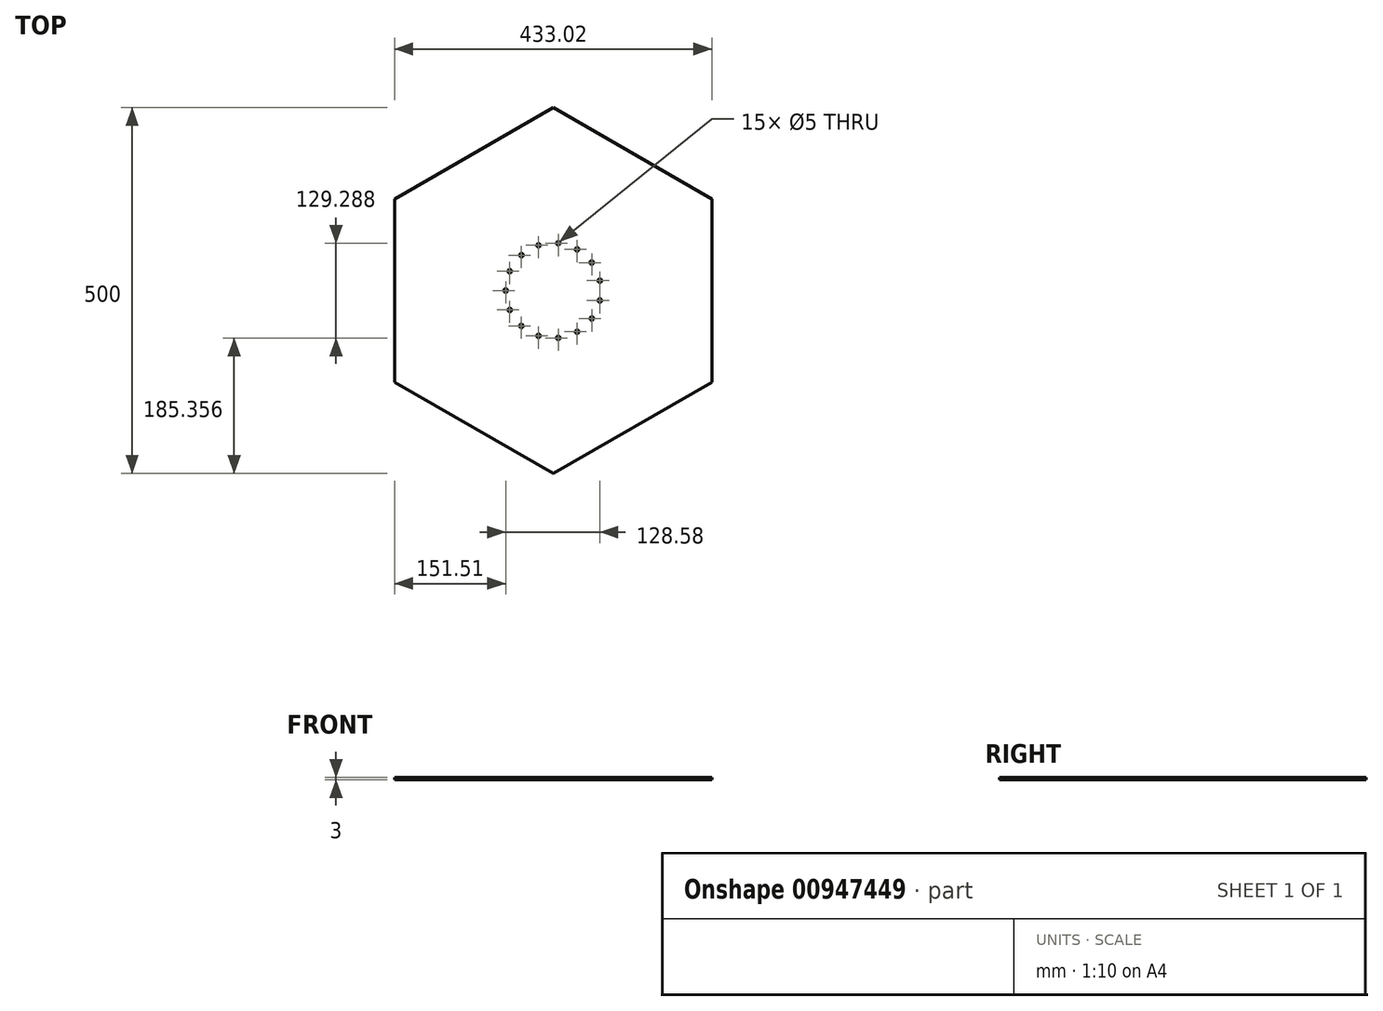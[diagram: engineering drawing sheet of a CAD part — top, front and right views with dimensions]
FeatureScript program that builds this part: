
annotation { "Feature Type Name" : "Feature", "Feature Type Description" : "" }
export const myFeature = defineFeature(function(context is Context, id is Id, definition is map)
    precondition{}
    {
        {
            var Q0;
            Q0=qCreatedBy(makeId("Top.planeOp"),FACE);
            var sketch = newSketch(context, id + "F0", { "sketchPlane" : qUnion([Q0])});
            skCircle(sketch, "E0", {"center": v(0, 0) * mm, "radius": 216.5 * mm});
            skCircle(sketch, "E1.cCircle", {"center": v(0, 0) * mm, "radius": 216.5 * mm, "construction": true});
            skLineSegment(sketch, "E1.0", {"start": v(216.5, 125) * mm, "end": v(216.5, -125) * mm});
            skLineSegment(sketch, "E1.1", {"start": v(216.5, -125) * mm, "end": v(0, -250) * mm});
            skLineSegment(sketch, "E1.2", {"start": v(0, -250) * mm, "end": v(-216.5, -125) * mm});
            skLineSegment(sketch, "E1.3", {"start": v(-216.5, -125) * mm, "end": v(-216.5, 125) * mm});
            skLineSegment(sketch, "E1.4", {"start": v(-216.5, 125) * mm, "end": v(0, 250) * mm});
            skLineSegment(sketch, "E1.5", {"start": v(0, 250) * mm, "end": v(216.5, 125) * mm});
            skPoint(sketch, "E1.0.midPoint", {"position": v(216.5, 0) * mm});
            skSolve(sketch);
        }
        {
            var Q0;
            Q0=makeQuery(id+"F0.imprint","IMPRINT",FACE,{"disambiguationData":[TD([[makeQuery(id+"F0.imprint","IMPRINT",EDGE,{"derivedFrom":sQuery(id+"F0.wireOp",EDGE,"E0")}),1.0]])]});
            var Q1;
            {var subQ0=sQuery(id+"F0.wireOp",EDGE,"E1.4");var subQ1=sQuery(id+"F0.wireOp",EDGE,"E0");var subQ2=makeQuery(id+"F0.imprint","INTERSECT",VERTEX,{"derivedFrom":[subQ1,subQ0]});Q1=makeQuery(id+"F0.imprint","IMPRINT",FACE,{"disambiguationData":[TD([[makeQuery(id+"F0.imprint","IMPRINT",EDGE,{"disambiguationData":[TD([[subQ2,-1.0]])],"derivedFrom":subQ1}),-1.0]])]});}
            var Q2;
            {var subQ0=sQuery(id+"F0.wireOp",EDGE,"E1.5");var subQ1=sQuery(id+"F0.wireOp",EDGE,"E0");var subQ2=makeQuery(id+"F0.imprint","INTERSECT",VERTEX,{"derivedFrom":[subQ1,subQ0]});Q2=makeQuery(id+"F0.imprint","IMPRINT",FACE,{"disambiguationData":[TD([[makeQuery(id+"F0.imprint","IMPRINT",EDGE,{"disambiguationData":[TD([[subQ2,-1.0]])],"derivedFrom":subQ1}),-1.0]])]});}
            var Q3;
            {var subQ0=sQuery(id+"F0.wireOp",EDGE,"E1.5");var subQ1=sQuery(id+"F0.wireOp",EDGE,"E0");var subQ2=makeQuery(id+"F0.imprint","INTERSECT",VERTEX,{"derivedFrom":[subQ1,subQ0]});Q3=makeQuery(id+"F0.imprint","IMPRINT",FACE,{"disambiguationData":[TD([[makeQuery(id+"F0.imprint","IMPRINT",EDGE,{"disambiguationData":[TD([[subQ2,1.0]])],"derivedFrom":subQ1}),-1.0]])]});}
            var Q4;
            {var subQ0=sQuery(id+"F0.wireOp",EDGE,"E1.0");var subQ1=sQuery(id+"F0.wireOp",EDGE,"E0");var subQ2=makeQuery(id+"F0.imprint","INTERSECT",VERTEX,{"derivedFrom":[subQ1,subQ0]});Q4=makeQuery(id+"F0.imprint","IMPRINT",FACE,{"disambiguationData":[TD([[makeQuery(id+"F0.imprint","IMPRINT",EDGE,{"disambiguationData":[TD([[subQ2,1.0]])],"derivedFrom":subQ1}),-1.0]])]});}
            var Q5;
            {var subQ0=sQuery(id+"F0.wireOp",EDGE,"E1.2");var subQ1=sQuery(id+"F0.wireOp",EDGE,"E0");var subQ2=makeQuery(id+"F0.imprint","INTERSECT",VERTEX,{"derivedFrom":[subQ1,subQ0]});Q5=makeQuery(id+"F0.imprint","IMPRINT",FACE,{"disambiguationData":[TD([[makeQuery(id+"F0.imprint","IMPRINT",EDGE,{"disambiguationData":[TD([[subQ2,-1.0]])],"derivedFrom":subQ1}),-1.0]])]});}
            var Q6;
            {var subQ0=sQuery(id+"F0.wireOp",EDGE,"E1.3");var subQ1=sQuery(id+"F0.wireOp",EDGE,"E0");var subQ2=makeQuery(id+"F0.imprint","INTERSECT",VERTEX,{"derivedFrom":[subQ1,subQ0]});Q6=makeQuery(id+"F0.imprint","IMPRINT",FACE,{"disambiguationData":[TD([[makeQuery(id+"F0.imprint","IMPRINT",EDGE,{"disambiguationData":[TD([[subQ2,-1.0]])],"derivedFrom":subQ1}),-1.0]])]});}
            extrude(context, id + "F1", {"entities" : qUnion([Q0, Q1, Q2, Q3, Q4, Q5, Q6]), "oppositeDirection" : true, "depth" : 3 * mm, "offsetDistance" : 25 * mm});
        }
        {
            var Q0;
            Q0=makeQuery(id+"F1.opExtrude","CAP_FACE",FACE,{"disambiguationData":[OSD([sQuery(id+"F0.wireOp",EDGE,"E1.0"),sQuery(id+"F0.wireOp",EDGE,"E1.1"),sQuery(id+"F0.wireOp",EDGE,"E1.2"),sQuery(id+"F0.wireOp",EDGE,"E1.3"),sQuery(id+"F0.wireOp",EDGE,"E1.4"),sQuery(id+"F0.wireOp",EDGE,"E1.5")])],"isStart":true});
            var sketch = newSketch(context, id + "F2", { "sketchPlane" : qUnion([Q0])});
            skCircle(sketch, "E2", {"center": v(0, 0) * mm, "radius": 65 * mm, "construction": true});
            skCircle(sketch, "E3", {"center": v(-65, 0) * mm, "radius": 2.5 * mm});
            skCircle(sketch, "E4.1.0", {"center": v(-59.38, -26.44) * mm, "radius": 2.5 * mm});
            skCircle(sketch, "E4.2.0", {"center": v(-43.5, -48.3) * mm, "radius": 2.5 * mm});
            skCircle(sketch, "E4.3.0", {"center": v(-20.09, -61.82) * mm, "radius": 2.5 * mm});
            skCircle(sketch, "E4.4.0", {"center": v(6.8, -64.64) * mm, "radius": 2.5 * mm});
            skCircle(sketch, "E4.5.0", {"center": v(32.5, -56.3) * mm, "radius": 2.5 * mm});
            skCircle(sketch, "E5.1.6.0", {"center": v(52.59, -38.2) * mm, "radius": 2.5 * mm});
            skCircle(sketch, "E5.1.7.0", {"center": v(63.58, -13.51) * mm, "radius": 2.5 * mm});
            skCircle(sketch, "E5.1.8.0", {"center": v(63.58, 13.51) * mm, "radius": 2.5 * mm});
            skCircle(sketch, "E5.1.9.0", {"center": v(52.59, 38.2) * mm, "radius": 2.5 * mm});
            skCircle(sketch, "E5.1.10.0", {"center": v(32.5, 56.3) * mm, "radius": 2.5 * mm});
            skCircle(sketch, "E5.1.11.0", {"center": v(6.8, 64.64) * mm, "radius": 2.5 * mm});
            skCircle(sketch, "E5.1.12.0", {"center": v(-20.09, 61.82) * mm, "radius": 2.5 * mm});
            skCircle(sketch, "E5.1.13.0", {"center": v(-43.5, 48.3) * mm, "radius": 2.5 * mm});
            skCircle(sketch, "E5.1.14.0", {"center": v(-59.38, 26.44) * mm, "radius": 2.5 * mm});
            skSolve(sketch);
        }
        {
            var Q0;
            Q0=makeQuery(id+"F2.imprint","IMPRINT",FACE,{"disambiguationData":[TD([[makeQuery(id+"F2.imprint","IMPRINT",EDGE,{"derivedFrom":sQuery(id+"F2.wireOp",EDGE,"E3")}),1.0]])]});
            var Q1;
            Q1=makeQuery(id+"F2.imprint","IMPRINT",FACE,{"disambiguationData":[TD([[makeQuery(id+"F2.imprint","IMPRINT",EDGE,{"derivedFrom":sQuery(id+"F2.wireOp",EDGE,"E4.5.0")}),1.0]])]});
            var Q2;
            Q2=makeQuery(id+"F2.imprint","IMPRINT",FACE,{"disambiguationData":[TD([[makeQuery(id+"F2.imprint","IMPRINT",EDGE,{"derivedFrom":sQuery(id+"F2.wireOp",EDGE,"E4.4.0")}),1.0]])]});
            var Q3;
            Q3=makeQuery(id+"F2.imprint","IMPRINT",FACE,{"disambiguationData":[TD([[makeQuery(id+"F2.imprint","IMPRINT",EDGE,{"derivedFrom":sQuery(id+"F2.wireOp",EDGE,"E4.3.0")}),1.0]])]});
            var Q4;
            Q4=makeQuery(id+"F2.imprint","IMPRINT",FACE,{"disambiguationData":[TD([[makeQuery(id+"F2.imprint","IMPRINT",EDGE,{"derivedFrom":sQuery(id+"F2.wireOp",EDGE,"E4.2.0")}),1.0]])]});
            var Q5;
            Q5=makeQuery(id+"F2.imprint","IMPRINT",FACE,{"disambiguationData":[TD([[makeQuery(id+"F2.imprint","IMPRINT",EDGE,{"derivedFrom":sQuery(id+"F2.wireOp",EDGE,"E4.1.0")}),1.0]])]});
            var Q6;
            Q6=makeQuery(id+"F2.imprint","IMPRINT",FACE,{"disambiguationData":[TD([[makeQuery(id+"F2.imprint","IMPRINT",EDGE,{"derivedFrom":sQuery(id+"F2.wireOp",EDGE,"E5.1.14.0")}),1.0]])]});
            var Q7;
            Q7=makeQuery(id+"F2.imprint","IMPRINT",FACE,{"disambiguationData":[TD([[makeQuery(id+"F2.imprint","IMPRINT",EDGE,{"derivedFrom":sQuery(id+"F2.wireOp",EDGE,"E5.1.13.0")}),1.0]])]});
            var Q8;
            Q8=makeQuery(id+"F2.imprint","IMPRINT",FACE,{"disambiguationData":[TD([[makeQuery(id+"F2.imprint","IMPRINT",EDGE,{"derivedFrom":sQuery(id+"F2.wireOp",EDGE,"E5.1.12.0")}),1.0]])]});
            var Q9;
            Q9=makeQuery(id+"F2.imprint","IMPRINT",FACE,{"disambiguationData":[TD([[makeQuery(id+"F2.imprint","IMPRINT",EDGE,{"derivedFrom":sQuery(id+"F2.wireOp",EDGE,"E5.1.11.0")}),1.0]])]});
            var Q10;
            Q10=makeQuery(id+"F2.imprint","IMPRINT",FACE,{"disambiguationData":[TD([[makeQuery(id+"F2.imprint","IMPRINT",EDGE,{"derivedFrom":sQuery(id+"F2.wireOp",EDGE,"E5.1.10.0")}),1.0]])]});
            var Q11;
            Q11=makeQuery(id+"F2.imprint","IMPRINT",FACE,{"disambiguationData":[TD([[makeQuery(id+"F2.imprint","IMPRINT",EDGE,{"derivedFrom":sQuery(id+"F2.wireOp",EDGE,"E5.1.9.0")}),1.0]])]});
            var Q12;
            Q12=makeQuery(id+"F2.imprint","IMPRINT",FACE,{"disambiguationData":[TD([[makeQuery(id+"F2.imprint","IMPRINT",EDGE,{"derivedFrom":sQuery(id+"F2.wireOp",EDGE,"E5.1.8.0")}),1.0]])]});
            var Q13;
            Q13=makeQuery(id+"F2.imprint","IMPRINT",FACE,{"disambiguationData":[TD([[makeQuery(id+"F2.imprint","IMPRINT",EDGE,{"derivedFrom":sQuery(id+"F2.wireOp",EDGE,"E5.1.7.0")}),1.0]])]});
            var Q14;
            Q14=makeQuery(id+"F2.imprint","IMPRINT",FACE,{"disambiguationData":[TD([[makeQuery(id+"F2.imprint","IMPRINT",EDGE,{"derivedFrom":sQuery(id+"F2.wireOp",EDGE,"E5.1.6.0")}),1.0]])]});
            extrude(context, id + "F3", {"entities" : qUnion([Q0, Q1, Q2, Q3, Q4, Q5, Q6, Q7, Q8, Q9, Q10, Q11, Q12, Q13, Q14]), "operationType" : NewBodyOperationType.REMOVE, "endBound" : BoundingType.UP_TO_NEXT, "oppositeDirection" : true, "depth" : 25 * mm, "offsetDistance" : 25 * mm});
        }
    });
